# Revit family: DB 160 ETL (new)
name_source: partatom
category: Lighting Fixtures
revit_build: Autodesk Revit 2018 (Build: 20170223_1515(x64)
units: mm (PartAtom-declared; Revit-internal decimal feet)

## family parameters
Always vertical = Yes
Cut with Voids When Loaded = No
Host = Wall
Light Source = Yes
OmniClass Number = 23.80.70.00
OmniClass Title = Lighting
Part Type = Normal
Room Calculation Point = No
Round Connector Dimension = Use Diameter
Shared = No

## types (3) — shared parameters
ADA compliant = NO
Color Filter = 16777215
Dimmable = No
Dimming Lamp Color Temperature Shift = <None>
Driver Included = Yes
Driver Required = No
Electrical Class = 1
Emit from Line Length = 610 mm
Lamp = LED
Length of Cable Supplied = 150 mm / 6 "
Light Source Fixed = yes
Location rating = WET
Main Material = Metal - Aluminium
Manufacturer = Astro Lighting Ltd
Photometric Web File = GNC-19579  7944 - Dunbar 160 LED White ies.ies
Product Location = Outdoor
Product Name = Dunbar 160
Tilt Angle = 0.00°
URL = www.astrolighting.com

## per-type parameters (varying)
| type | Efficacy (lm/w) | Main Finish | Power (Watts) | Product Code | Product SKU |
| Dunbar 160 - Textured White | 41.4 | Textured White | 6.0 | 8088 | 1384013 |
| Dunbar 160 - Textured Grey | 23.3 | Textured Grey | 5.8 | 8090 | 1384015 |
| Dunbar 160 - Textured Black | 18.7 | Textured Black | 6.0 | 8089 | 1384014 |

## geometry (parser evidence)
native form markers: Sweep x3
no freeform markers — native parametric forms only
